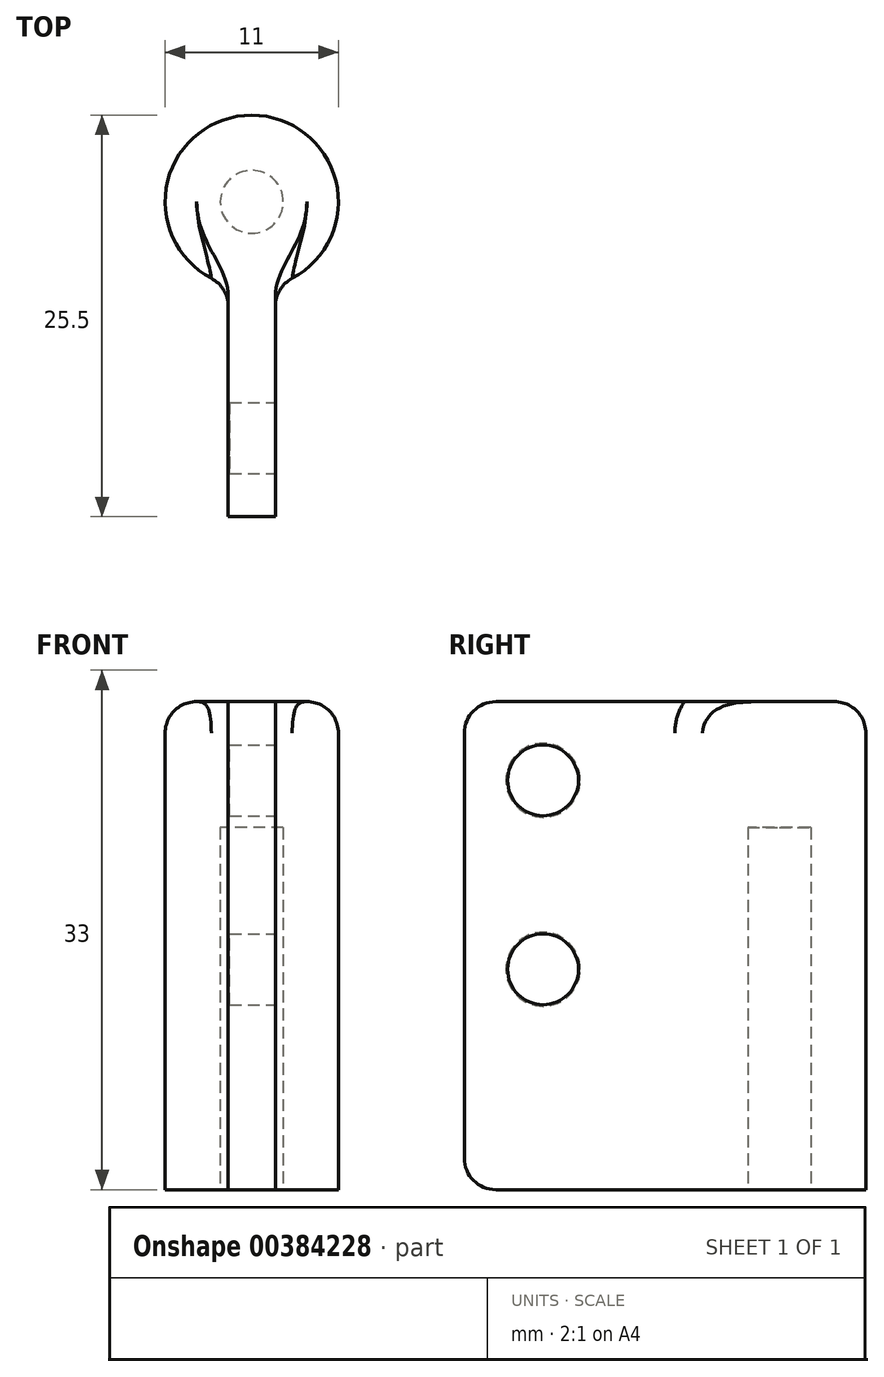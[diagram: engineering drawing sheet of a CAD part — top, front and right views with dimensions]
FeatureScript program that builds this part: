
annotation { "Feature Type Name" : "Feature", "Feature Type Description" : "" }
export const myFeature = defineFeature(function(context is Context, id is Id, definition is map)
    precondition{}
    {
        {
            var Q0;
            Q0=qCreatedBy(makeId("Top.planeOp"),FACE);
            var sketch = newSketch(context, id + "F0", { "sketchPlane" : qUnion([Q0])});
            skArc(sketch, "E0", {"start": v(1.5, -5.3) * mm, "mid": v(0, 5.5) * mm, "end": v(-1.5, -5.3) * mm});
            skCircle(sketch, "E1", {"center": v(0, 0) * mm, "radius": 2 * mm});
            skLineSegment(sketch, "E2.top", {"start": v(1.5, -20) * mm, "end": v(-1.5, -20) * mm});
            skLineSegment(sketch, "E2.left", {"start": v(1.5, -5.3) * mm, "end": v(1.5, -20) * mm});
            skLineSegment(sketch, "E2.right", {"start": v(-1.5, -5.3) * mm, "end": v(-1.5, -20) * mm});
            skLineSegment(sketch, "E3", {"start": v(0, 0) * mm, "end": v(0, -30.7) * mm, "construction": true});
            skSolve(sketch);
        }
        {
            var Q0;
            Q0 = qSketchRegion(id + "F0", true);
            extrude(context, id + "F1", {"entities" : qUnion([Q0]), "depth" : 31 * mm});
        }
        {
            var Q0;
            Q0=makeQuery(id+"F1.opExtrude","CAP_FACE",FACE,{"disambiguationData":[OSD([sQuery(id+"F0.wireOp",EDGE,"E0"),sQuery(id+"F0.wireOp",EDGE,"E1")])],"isStart":false});
            var sketch = newSketch(context, id + "F2", { "sketchPlane" : qUnion([Q0])});
            skCircle(sketch, "E4", {"center": v(0, 0) * mm, "radius": 2 * mm});
            skSolve(sketch);
        }
        {
            var Q0;
            Q0=makeQuery(id+"F2.imprint","IMPRINT",FACE,{"disambiguationData":[TD([[makeQuery(id+"F2.imprint","IMPRINT",EDGE,{"derivedFrom":sQuery(id+"F2.wireOp",EDGE,"E4")}),1.0]])]});
            extrude(context, id + "F3", {"entities" : qUnion([Q0]), "operationType" : NewBodyOperationType.ADD, "oppositeDirection" : true, "depth" : 8 * mm});
        }
        {
            var Q0;
            Q0=makeQuery(id+"F1.opExtrude","SWEPT_FACE",FACE,{"disambiguationData":[OSD([sQuery(id+"F0.wireOp",EDGE,"E2.left")])]});
            var sketch = newSketch(context, id + "F4", { "sketchPlane" : qUnion([Q0])});
            skCircle(sketch, "E5", {"center": v(-15, 14) * mm, "radius": 2.25 * mm});
            skCircle(sketch, "E6", {"center": v(-15, 26) * mm, "radius": 2.25 * mm});
            skLineSegment(sketch, "E7", {"start": v(-15, 36) * mm, "end": v(-15, -4.03) * mm, "construction": true});
            skSolve(sketch);
        }
        {
            var Q0;
            Q0 = qSketchRegion(id + "F4", true);
            extrude(context, id + "F5", {"entities" : qUnion([Q0]), "operationType" : NewBodyOperationType.REMOVE, "oppositeDirection" : true, "depth" : 25 * mm});
        }
        {
            var Q0;
            Q0=makeQuery(id+"F5.boolean.opBoolean","COPY",EDGE,{"derivedFrom":makeQuery(id+"F5.opExtrude","CAP_EDGE",EDGE,{"disambiguationData":[OSD([sQuery(id+"F4.wireOp",EDGE,"E6")])],"isStart":true})});
            var Q1;
            Q1=makeQuery(id+"F5.boolean.opBoolean","COPY",EDGE,{"derivedFrom":makeQuery(id+"F5.opExtrude","CAP_EDGE",EDGE,{"disambiguationData":[OSD([sQuery(id+"F4.wireOp",EDGE,"E5")])],"isStart":true})});
            var Q2;
            Q2=makeQuery(id+"F5.boolean.opBoolean","INTERSECT",EDGE,{"derivedFrom":[makeQuery(id+"F1.opExtrude","SWEPT_FACE",FACE,{"disambiguationData":[OSD([sQuery(id+"F0.wireOp",EDGE,"E2.right")])]}),makeQuery(id+"F5.opExtrude","SWEPT_FACE",FACE,{"disambiguationData":[OSD([sQuery(id+"F4.wireOp",EDGE,"E6")])]})]});
            var Q3;
            Q3=makeQuery(id+"F5.boolean.opBoolean","INTERSECT",EDGE,{"derivedFrom":[makeQuery(id+"F1.opExtrude","SWEPT_FACE",FACE,{"disambiguationData":[OSD([sQuery(id+"F0.wireOp",EDGE,"E2.right")])]}),makeQuery(id+"F5.opExtrude","SWEPT_FACE",FACE,{"disambiguationData":[OSD([sQuery(id+"F4.wireOp",EDGE,"E5")])]})]});
            chamfer(context, id + "F6", {"entities" : qUnion([Q0, Q1, Q2, Q3]), "width" : 0.1 * mm, "tangentPropagation" : true});
        }
        {
            var Q0;
            Q0=makeQuery(id+"F1.opExtrude","CAP_EDGE",EDGE,{"disambiguationData":[OSD([sQuery(id+"F0.wireOp",EDGE,"E0")])],"isStart":false});
            var Q1;
            Q1=makeQuery(id+"F1.opExtrude","CAP_EDGE",EDGE,{"disambiguationData":[OSD([sQuery(id+"F0.wireOp",EDGE,"E2.top")])],"isStart":false});
            var Q2;
            Q2=makeQuery(id+"F1.opExtrude","CAP_EDGE",EDGE,{"disambiguationData":[OSD([sQuery(id+"F0.wireOp",EDGE,"E2.top")])],"isStart":true});
            fillet(context, id + "F7", {"entities" : qUnion([Q0, Q1, Q2]), "radius" : 2 * mm, "tangentPropagation" : true, "allowEdgeOverflow" : false});
        }
        {
            var Q0;
            Q0=makeQuery(id+"F1.opExtrude","SWEPT_EDGE",EDGE,{"disambiguationData":[OSD([sQuery(id+"F0.wireOp",EDGE,"E0"),sQuery(id+"F0.wireOp",EDGE,"E2.left")])]});
            var Q1;
            Q1=makeQuery(id+"F1.opExtrude","SWEPT_EDGE",EDGE,{"disambiguationData":[OSD([sQuery(id+"F0.wireOp",EDGE,"E0"),sQuery(id+"F0.wireOp",EDGE,"E2.right")])]});
            fillet(context, id + "F8", {"entities" : qUnion([Q0, Q1]), "radius" : 2 * mm, "tangentPropagation" : true, "allowEdgeOverflow" : false});
        }
    });
